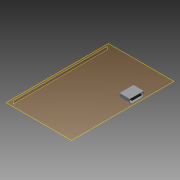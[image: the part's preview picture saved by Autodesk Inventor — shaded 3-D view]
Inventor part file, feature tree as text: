
AUTODESK INVENTOR PART (.ipt)
format: ipt  version: 2013 SP2 (Build 170200200, 200)  size: 107,520 bytes
history: native  units: mm
features: plane x2, extrude x2, sketch x2, chamfer x1, shell x1
ambient origin geometry x8: Origin, YZ Plane, XZ Plane, XY Plane, X Axis, Y Axis, Z Axis, Center Point
bodies: Solid1 (feature_tree)
feature tree (8):
  plane  "Work Plane1"
  plane  "Work Plane2"
  extrude  "Extrusion1"  Depth=15.0mm
  chamfer  "Chamfer1"  Distance=5.6mm
  shell  "Shell1"  Thickness=0.3mm
  extrude  "Extrusion2"  Depth=1.0mm
  sketch  "Sketch1"  dims[d0=11.0mm d2=15.0mm d3=5.6mm d4=0.0mm]
  sketch  "Sketch2"  dims[d5=2.0mm d6=2.0mm d7=45.0deg d8=0.3mm d9=1.0mm d12=2.0mm d13=2.0mm d14=1.6mm d15=5.6mm d16=0.0mm]
